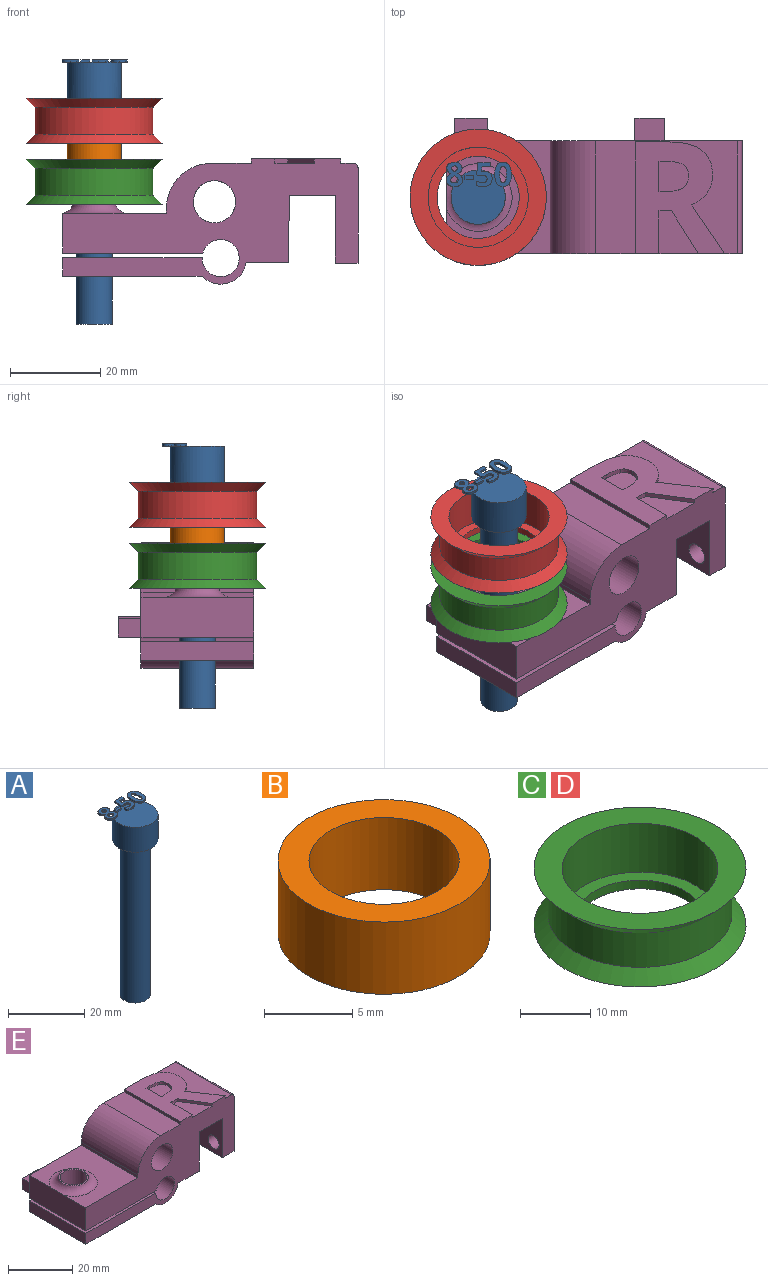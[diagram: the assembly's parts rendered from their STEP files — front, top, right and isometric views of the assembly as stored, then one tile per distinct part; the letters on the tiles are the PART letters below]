
ASSEMBLY  parts=5 mates=4
PART A: 86 faces, bbox 14.5x13.7x58.5 mm
  f0: plane 12x12mm, normal (0,0,1), area 99.4mm2, adj f5,f22,f23,f24,f25,f26,f40,f41
  f1: plane 1x0.26mm, normal (0,0,1), area 0.1mm2, adj f5,f46,f47,f48,f49
  f2: plane 0.85x0.68mm, normal (0,0,1), area 0.2mm2, adj f5,f29,f30,f31
  f3: cylinder r=4mm len=50mm, axis (0,0,-1), area 1256.6mm2, adj f4,f6
  f4: plane 8x8mm, normal (0,0,-1), area 50.3mm2, adj f3
  f5: cylinder r=6mm len=12mm, axis (0,0,-1), area 301.6mm2, adj f0,f1,f2,f6,f39,f45,f67,f85
  f6: plane 12x12mm, normal (0,0,-1), area 62.8mm2, adj f3,f5
  f7: extruded ~0.5x0.46mm, area 0.2mm2, adj f8,f37,f38,f39
  f8: extruded ~0.5x0.46mm, area 0.2mm2, adj f7,f9,f38,f39
  f9: extruded ~0.5x0.39mm, area 0.2mm2, adj f8,f10,f38,f39
  f10: extruded ~0.5x0.4mm, area 0.2mm2, adj f9,f11,f38,f39
  f11: extruded ~0.5x0.49mm, area 0.3mm2, adj f10,f12,f38,f39
  f12: extruded ~0.5x0.5mm, area 0.3mm2, adj f11,f13,f38,f39
  f13: extruded ~0.5x0.39mm, area 0.2mm2, adj f12,f37,f38,f39
  f14: extruded ~1.22x0.5mm, area 0.6mm2, adj f15,f35,f38,f39
  f15: extruded ~1.22x0.5mm, area 0.6mm2, adj f14,f16,f38,f39
  f16: extruded ~0.91x0.5mm, area 0.5mm2, adj f15,f17,f38,f39
  f17: extruded ~0.71x0.5mm, area 0.4mm2, adj f16,f18,f38,f39
  f18: extruded ~0.65x0.61mm, area 0.4mm2, adj f17,f19,f38,f39
  f19: extruded ~0.77x0.62mm, area 0.5mm2, adj f18,f20,f38,f39
  f20: extruded ~0.8x0.5mm, area 0.4mm2, adj f19,f21,f38,f39
  f21: extruded ~1.04x0.5mm, area 0.6mm2, adj f20,f22,f38,f39
  f22: extruded ~1.36x0.5mm, area 0.7mm2, adj f0,f21,f23,f38,f39
  f23: extruded ~1.33x0.5mm, area 0.7mm2, adj f0,f22,f24,f38
  f24: extruded ~1.04x0.51mm, area 0.6mm2, adj f0,f23,f25,f38
  f25: extruded ~0.75x0.5mm, area 0.4mm2, adj f0,f24,f26,f38
  f26: extruded ~0.85x0.66mm, area 0.5mm2, adj f0,f25,f27,f38,f39
  f27: extruded ~0.72x0.56mm, area 0.5mm2, adj f26,f28,f38,f39
  f28: extruded ~0.72x0.5mm, area 0.4mm2, adj f27,f35,f38,f39
  f29: extruded ~0.5x0.45mm, area 0.3mm2, adj f2,f30,f36,f38,f39
  f30: extruded ~0.5x0.47mm, area 0.3mm2, adj f2,f29,f31,f38
  f31: extruded ~0.62x0.5mm, area 0.3mm2, adj f2,f30,f32,f38,f39
  f32: extruded ~0.59x0.5mm, area 0.3mm2, adj f31,f33,f38,f39
  f33: extruded ~0.5x0.48mm, area 0.3mm2, adj f32,f34,f38,f39
  f34: extruded ~0.89x0.77mm, area 0.6mm2, adj f33,f36,f38,f39
  f35: extruded ~0.93x0.5mm, area 0.5mm2, adj f14,f28,f38,f39
  f36: extruded ~0.66x0.5mm, area 0.4mm2, adj f29,f34,f38,f39
  f37: extruded ~0.5x0.39mm, area 0.2mm2, adj f7,f13,f38,f39
  f38: plane 5.4x3.69mm, normal (0,0,1), area 12.7mm2, adj f7,f8,f9,f10,f11,f12,f13,f14
  f39: plane 5.4x3.53mm, normal (0,0,-1), area 10.2mm2, adj f5,f7,f8,f9,f10,f11,f12,f13
  f40: plane 0.9x0.5mm, normal (-1,0,0), area 0.4mm2, adj f0,f41,f43,f44
  f41: plane 1.93x0.5mm, normal (0,-1,0), area 1mm2, adj f0,f40,f42,f44
  f42: plane 0.9x0.5mm, normal (1,0,0), area 0.4mm2, adj f0,f41,f43,f44
  f43: plane 1.93x0.5mm, normal (0,1,0), area 1mm2, adj f0,f40,f42,f44
  f44: plane 1.93x0.9mm, normal (0,0,1), area 1.7mm2, adj f40,f41,f42,f43
  f45: plane 0.76x0.31mm, normal (0,0,-1), area 0mm2, adj f5,f46
  f46: extruded ~1.21x0.5mm, area 0.7mm2, adj f0,f1,f45,f47,f65,f66
  f47: extruded ~0.54x0.5mm, area 0.3mm2, adj f1,f46,f48,f66
  f48: plane 0.5x0.13mm, normal (-0.2,0.98,0), area 0.1mm2, adj f1,f47,f49,f66
  f49: plane 1.03x0.5mm, normal (1,-0.09,0), area 0.5mm2, adj f1,f48,f50,f66,f67
  f50: plane 1.88x0.5mm, normal (0,-1,0), area 0.9mm2, adj f49,f51,f66,f67
  f51: plane 0.94x0.5mm, normal (1,0,0), area 0.5mm2, adj f50,f52,f66,f67
  f52: plane 2.85x0.5mm, normal (0,1,0), area 1.4mm2, adj f51,f53,f66,f67
  f53: plane 2.68x0.5mm, normal (-1,0.07,0), area 1.3mm2, adj f0,f52,f54,f66,f67
  f54: plane 0.5x0.44mm, normal (-0.47,-0.88,0), area 0.3mm2, adj f0,f53,f55,f66
  f55: extruded ~0.5x0.37mm, area 0.2mm2, adj f0,f54,f56,f66
  f56: extruded ~0.5x0.42mm, area 0.2mm2, adj f0,f55,f57,f66
  f57: extruded ~1.05x0.8mm, area 0.8mm2, adj f0,f56,f58,f66
  f58: extruded ~1.02x0.83mm, area 0.8mm2, adj f0,f57,f59,f66
  f59: extruded ~0.72x0.5mm, area 0.4mm2, adj f0,f58,f60,f66
  f60: extruded ~0.66x0.5mm, area 0.4mm2, adj f0,f59,f61,f66
  f61: plane 0.96x0.5mm, normal (-1,0,0), area 0.5mm2, adj f0,f60,f62,f66
  f62: extruded ~1.42x0.5mm, area 0.7mm2, adj f0,f61,f63,f66
  f63: extruded ~1.55x0.5mm, area 0.8mm2, adj f0,f62,f64,f66
  f64: extruded ~1.36x0.54mm, area 0.8mm2, adj f0,f63,f65,f66
  f65: extruded ~1.17x0.5mm, area 0.6mm2, adj f0,f46,f64,f66
  f66: plane 5.33x3.51mm, normal (0,0,1), area 10.9mm2, adj f46,f47,f48,f49,f50,f51,f52,f53
  f67: plane 2.97x1.71mm, normal (0,0,-1), area 3.5mm2, adj f5,f49,f50,f51,f52,f53
  f68: extruded ~1.39x0.5mm, area 0.7mm2, adj f69,f83,f84,f85
  f69: extruded ~1.39x0.5mm, area 0.7mm2, adj f68,f70,f84,f85
  f70: extruded ~0.56x0.5mm, area 0.4mm2, adj f69,f71,f84,f85
  f71: extruded ~0.56x0.5mm, area 0.4mm2, adj f70,f72,f84,f85
  f72: extruded ~1.39x0.5mm, area 0.7mm2, adj f71,f73,f84,f85
  f73: extruded ~1.38x0.5mm, area 0.7mm2, adj f72,f74,f84,f85
  f74: extruded ~0.56x0.5mm, area 0.4mm2, adj f73,f83,f84,f85
  f75: extruded ~2.04x0.5mm, area 1.1mm2, adj f76,f82,f84,f85
  f76: extruded ~2.02x0.5mm, area 1.1mm2, adj f75,f77,f84,f85
  f77: extruded ~1.38x0.69mm, area 0.8mm2, adj f76,f78,f84,f85
  f78: extruded ~1.38x0.66mm, area 0.8mm2, adj f77,f79,f84,f85
  f79: extruded ~2.05x0.5mm, area 1.1mm2, adj f78,f80,f84,f85
  f80: extruded ~2.02x0.5mm, area 1mm2, adj f0,f79,f81,f84,f85
  f81: extruded ~1.37x0.68mm, area 0.8mm2, adj f0,f80,f82,f84
  f82: extruded ~1.39x0.66mm, area 0.8mm2, adj f0,f75,f81,f84,f85
  f83: extruded ~0.56x0.5mm, area 0.4mm2, adj f68,f74,f84,f85
  f84: plane 5.41x3.68mm, normal (0,0,1), area 12.1mm2, adj f68,f69,f70,f71,f72,f73,f74,f75
  f85: plane 5.41x3.68mm, normal (0,0,-1), area 10.3mm2, adj f5,f68,f69,f70,f71,f72,f73,f74
PART B: 4 faces, bbox 12x12x5 mm
  f0: cylinder r=4.25mm len=8.5mm, axis (0,0,-1), area 133.5mm2, adj f2,f3
  f1: cylinder r=6mm len=12mm, axis (0,0,-1), area 188.5mm2, adj f2,f3
  f2: plane 12x12mm, normal (0,0,1), area 56.4mm2, adj f0,f1
  f3: plane 12x12mm, normal (0,0,-1), area 56.4mm2, adj f0,f1
PART C: 8 faces, bbox 30.2x30.2x10 mm
  f0: plane 30.2x30.2mm, normal (0,0,1), area 329.2mm2, adj f1,f7
  f1: cylinder r=11.1mm len=22.2mm, axis (0,0,-1), area 592.8mm2, adj f0,f2
  f2: plane 22.2x22.2mm, normal (0,0,1), area 126.9mm2, adj f1,f3
  f3: cylinder r=9.1mm len=18.2mm, axis (0,0,-1), area 85.8mm2, adj f2,f4
  f4: plane 30.2x30.2mm, normal (0,0,-1), area 456.2mm2, adj f3,f5
  f5: cone r=13.1mm half-angle=45deg, axis (0,0,-1), area 250.6mm2, adj f4,f6
  f6: cylinder r=13.1mm len=26.2mm, axis (0,0,-1), area 493.9mm2, adj f5,f7
  f7: cone r=15.1mm half-angle=45deg, axis (0,0,1), area 250.6mm2, adj f0,f6
PART D: same geometry as C
PART E: 56 faces, bbox 68.9x30x27.7 mm
  f0: plane 31.42x25mm, normal (0,0,1), area 392.1mm2, adj f14,f15,f25,f27,f40,f41,f42,f43
  f1: plane 9.51x8.71mm, normal (0,0,1), area 54.7mm2, adj f14,f37,f38,f39
  f2: plane 25x4.12mm, normal (-1,0,0), area 103mm2, adj f5,f14,f15,f19
  f3: cylinder r=4.17mm len=8.35mm, axis (0,0,1), area 108.1mm2, adj f5,f19
  f4: plane 25x9.34mm, normal (0,0,-1), area 233.4mm2, adj f13,f14,f15,f17
  f5: plane 30.88x25mm, normal (0,0,-1), area 717.2mm2, adj f2,f3,f14,f15,f17
  f6: plane 25x8.82mm, normal (-1,0,0), area 219.6mm2, adj f7,f14,f15,f20,f24
  f7: plane 25x23mm, normal (0,0,1), area 400mm2, adj f6,f8,f14,f15,f24
  f8: plane 25x1.1mm, normal (-1,0,0), area 27.5mm2, adj f7,f14,f15,f25
  f9: plane 25x21.09mm, normal (1,0,0), area 493.5mm2, adj f10,f14,f15,f22,f23,f27
  f10: plane 25x5mm, normal (0,0,-1), area 125mm2, adj f9,f11,f14,f15
  f11: plane 25x15mm, normal (-1,0,0), area 341.3mm2, adj f10,f12,f14,f15,f22,f23
  f12: plane 25x10.2mm, normal (0,0,-1), area 255mm2, adj f11,f13,f14,f15
  f13: plane 25x14.91mm, normal (1,0,-0.01), area 372.8mm2, adj f4,f12,f14,f15
  f14: plane 65.42x27.75mm, normal (0,-1,0), area 997.9mm2, adj f0,f1,f2,f4,f5,f6,f7,f8
  f15: plane 65.42x26.75mm, normal (0,1,0), area 926.8mm2, adj f0,f2,f4,f5,f6,f7,f8,f9
  f16: cylinder r=4.17mm len=10.78mm, axis (0,0,1), area 282.8mm2, adj f20,f21
  f17: cylinder r=5.75mm len=25mm, axis (0,-1,0), area 315.9mm2, adj f4,f5,f14,f15
  f18: cylinder r=4.1mm len=25mm, axis (0,-1,0), area 618.7mm2, adj f14,f15,f19,f20
  f19: plane 30.91x25mm, normal (0,0,1), area 718.1mm2, adj f2,f3,f14,f15,f18
  f20: plane 31.07x30mm, normal (0,0,-1), area 758.4mm2, adj f6,f14,f15,f16,f18,f29,f30,f31
  f21: plane 9.35x9.35mm, normal (0,0,1), area 13.9mm2, adj f16,f24
  f22: cylinder r=2.43mm len=5mm, axis (1,0,0), area 76.2mm2, adj f9,f11
  f23: cylinder r=2.2mm len=5mm, axis (1,0,0), area 69.1mm2, adj f9,f11
  f24: torus R=7.5mm, axis (0,0,-1), area 134.6mm2, adj f6,f7,f21
  f25: cylinder r=10mm len=25mm, axis (0,-1,0), area 392.7mm2, adj f0,f8,f14,f15
  f26: cylinder r=4.68mm len=25mm, axis (0,-1,0), area 735.2mm2, adj f14,f15
  f27: cylinder r=1mm len=25mm, axis (0,-1,0), area 39.3mm2, adj f0,f9,f14,f15
  f28: plane 7.3x5mm, normal (0,0,1), area 36.5mm2, adj f15,f29,f30,f31
  f29: plane 5x4.12mm, normal (-1,0,0), area 20.6mm2, adj f15,f20,f28,f31
  f30: plane 5x4.12mm, normal (1,0,0), area 20.6mm2, adj f15,f20,f28,f31
  f31: plane 7.3x4.12mm, normal (0,1,0), area 30.1mm2, adj f20,f28,f29,f30
  f32: plane 6.63x5mm, normal (0,0,1), area 33.2mm2, adj f15,f33,f35,f36
  f33: plane 5x4.5mm, normal (-1,0,0), area 22.5mm2, adj f15,f32,f34,f36
  f34: plane 6.63x5mm, normal (0,0,-1), area 33.2mm2, adj f15,f33,f35,f36
  f35: plane 5x4.5mm, normal (1,0,0), area 22.5mm2, adj f15,f32,f34,f36
  f36: plane 6.63x4.5mm, normal (0,1,0), area 29.9mm2, adj f32,f33,f34,f35
  f37: plane 9.51x1mm, normal (1,0,0), area 9.5mm2, adj f1,f14,f38,f54
  f38: plane 2.79x1mm, normal (0,-1,0), area 2.8mm2, adj f1,f37,f39,f54
  f39: plane 9.51x5.92mm, normal (-0.85,-0.53,0), area 11.2mm2, adj f1,f14,f38,f54
  f40: extruded ~10.8x7.29mm, area 13mm2, adj f0,f14,f41,f54
  f41: extruded ~3.41x2.67mm, area 4.4mm2, adj f0,f40,f42,f54
  f42: extruded ~3.89x1.2mm, area 4.1mm2, adj f0,f41,f43,f54
  f43: extruded ~5.59x2.42mm, area 6.3mm2, adj f0,f42,f44,f54
  f44: extruded ~7.48x1.84mm, area 7.8mm2, adj f0,f43,f45,f54
  f45: plane 7.22x1mm, normal (0,1,0), area 7.2mm2, adj f0,f44,f46,f54
  f46: plane 24.79x1mm, normal (-1,0,0), area 24.8mm2, adj f0,f14,f45,f54
  f47: plane 1.69x1mm, normal (0,1,0), area 1.7mm2, adj f48,f53,f54,f55
  f48: plane 6.7x1mm, normal (1,0,0), area 6.7mm2, adj f47,f49,f54,f55
  f49: plane 1.6x1mm, normal (0,-1,0), area 1.6mm2, adj f48,f50,f54,f55
  f50: extruded ~3.75x1mm, area 3.9mm2, adj f49,f51,f54,f55
  f51: extruded ~2.51x1.21mm, area 2.9mm2, adj f50,f52,f54,f55
  f52: extruded ~2.61x1.19mm, area 3mm2, adj f51,f53,f54,f55
  f53: extruded ~3.68x1mm, area 3.8mm2, adj f47,f52,f54,f55
  f54: plane 24.79x19.8mm, normal (0,0,1), area 300mm2, adj f14,f37,f38,f39,f40,f41,f42,f43
  f55: plane 6.7x6.56mm, normal (0,0,1), area 38.8mm2, adj f47,f48,f49,f50,f51,f52,f53
PLACE A t=(-103.78,-12.5,-13.6)mm
PLACE B rot(axis=(1,0,0),180deg) t=(-103.78,-12.5,26.4)mm
PLACE C t=(-103.78,-12.5,18.1)mm
PLACE D t=(-103.78,-12.5,31.6)mm
PLACE E at identity
MATE fastened A.f3 <-> D.f1  axis (0,0,-1) through (-103.78,-12.5,36.4)mm
MATE fastened B.f0 <-> C.f1  axis (0,0,1) through (-103.78,-12.5,21.4)mm
MATE fastened C.f1 <-> E.f3  axis (0,0,-1) through (-103.78,-12.5,12.9)mm
MATE fastened D.f1 <-> B.f0  axis (0,0,-1) through (-103.78,-12.5,26.4)mm
